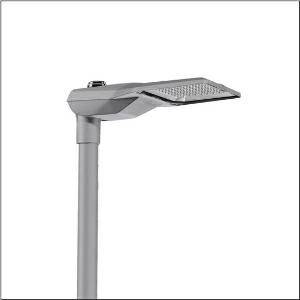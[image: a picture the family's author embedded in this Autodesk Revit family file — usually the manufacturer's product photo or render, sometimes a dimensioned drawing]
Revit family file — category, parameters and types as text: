
# Revit family: streetlight_sl_21_midi___st1_0a_5xe7d37n08lb_8a93
name_source: partatom
category: Lighting Fixtures
units: mm (PartAtom-declared; Revit-internal decimal feet)

## family parameters
Cut with Voids When Loaded = No
Host = Face
Light Source = No
Part Type = Normal
Room Calculation Point = No
Round Connector Dimension = Use Diameter
Shared = No

## types (1)
- --- (1 x LED, 14340 lm, 98.3 W, 3000K)
    Apparent Load = 98 VA
    CIE Flux Codes = 37 72 97 100 100
    Color Rendering = 70
    Color Temperature = 3000K
    Default Elevation = 1800 mm
    Description = Streetlight SL 21 midi, mast luminaire, primary light control with lens, of PMMA, primary optical cover: cover, of toughened safety glass, transparent, light distribution: ST1.0a, light emission: direct distribution, primary light characteristic: asymmetric, installation type: side-entry, LED, 3G 2.5mm², High Power LED, rated luminous flux: 14.340lm, luminous efficacy: 146lm/W, light colour: 730, colour temperature: 3000K, control: overheat protection, presetting dimming linear, constant luminous flux control, time-dependent luminous flux control, flexible luminous flux parameterisation, mains connection: 220..240V, AC, 50/60Hz, connection cable pre-assembled, cable length: 10,5m, wiring characteristics: H05VV-F, start of lifetime: 98W, end of service life: 101W, reduction: 45W, luminaire housing, of diecast aluminium (EN AC-44300), powder-coated, Siteco® metallic grey (DB 702S), corrosivity category C5 mid according to DIN EN ISO 12944, multi-level sealing system, sealing non-destructively replaceable, inclination adjustable: 0°, 5°, 10°, 15°, length: 644mm, width: 335mm, height: 110mm, spigot size: 42mm (side-entry), protection rating (complete): IP66, insulation class (complete): insulation class I (protective earthing), certification: CE, ENEC, ENEC+, VDE, impact resistance: IK09, permissible operating ambient temperature for outdoor applications: -40..+50°C, standard-compliant lighting for roads and squares, packaging unit: 1 piece

Light Distribution: ST1.0a
    Height = 111 mm
    Lamp = 1 x LED
    Lamp Light Flux = 14340 lm
    Lamp Power = 98.3 W
    Lamp count = 1
    Length = 644 mm
    Luminous efficacy = 146 lm/W
    Manufacturer = Siteco
    ModVariant = No
    Model = 5XE7D37N08LB
    Number of Poles = 1
    OnlyDefault = Yes
    Power Factor = 1
    Product Name = Streetlight SL 21 midi | ST1.0a
    Product group = mast luminaire | pylon top
    ProductGroupID = 6100
    Protection Class = Protection class I
    Protection Degree = IP 66
    RLX_Detail_Level = 1
    RLX_Emergency_Light_Flux = 0 lm
    RLX_Emergency_Type = 0
    RLX_Emergency_Type_DB = No
    RlxData = <blob elided: 90321 chars, md5=6bf38d37>
    Socket = socket
    Standby Power = 0 W
    System Light Flux = 14340 lm
    System Power = 98 W
    Type Comments = factory setting: luminous flux: 100 % | dim-lin: 254 | 1020 mA
    Type Image = l_1294377.jpg
    URL = http://relux.com
    VarID = @adj_067419
    Voltage = 0 V
    Weight = 0.00 kg
    Width = 336 mm

## geometry (parser evidence)
native form markers: Blend x4, Sweep x12
no freeform markers — native parametric forms only
